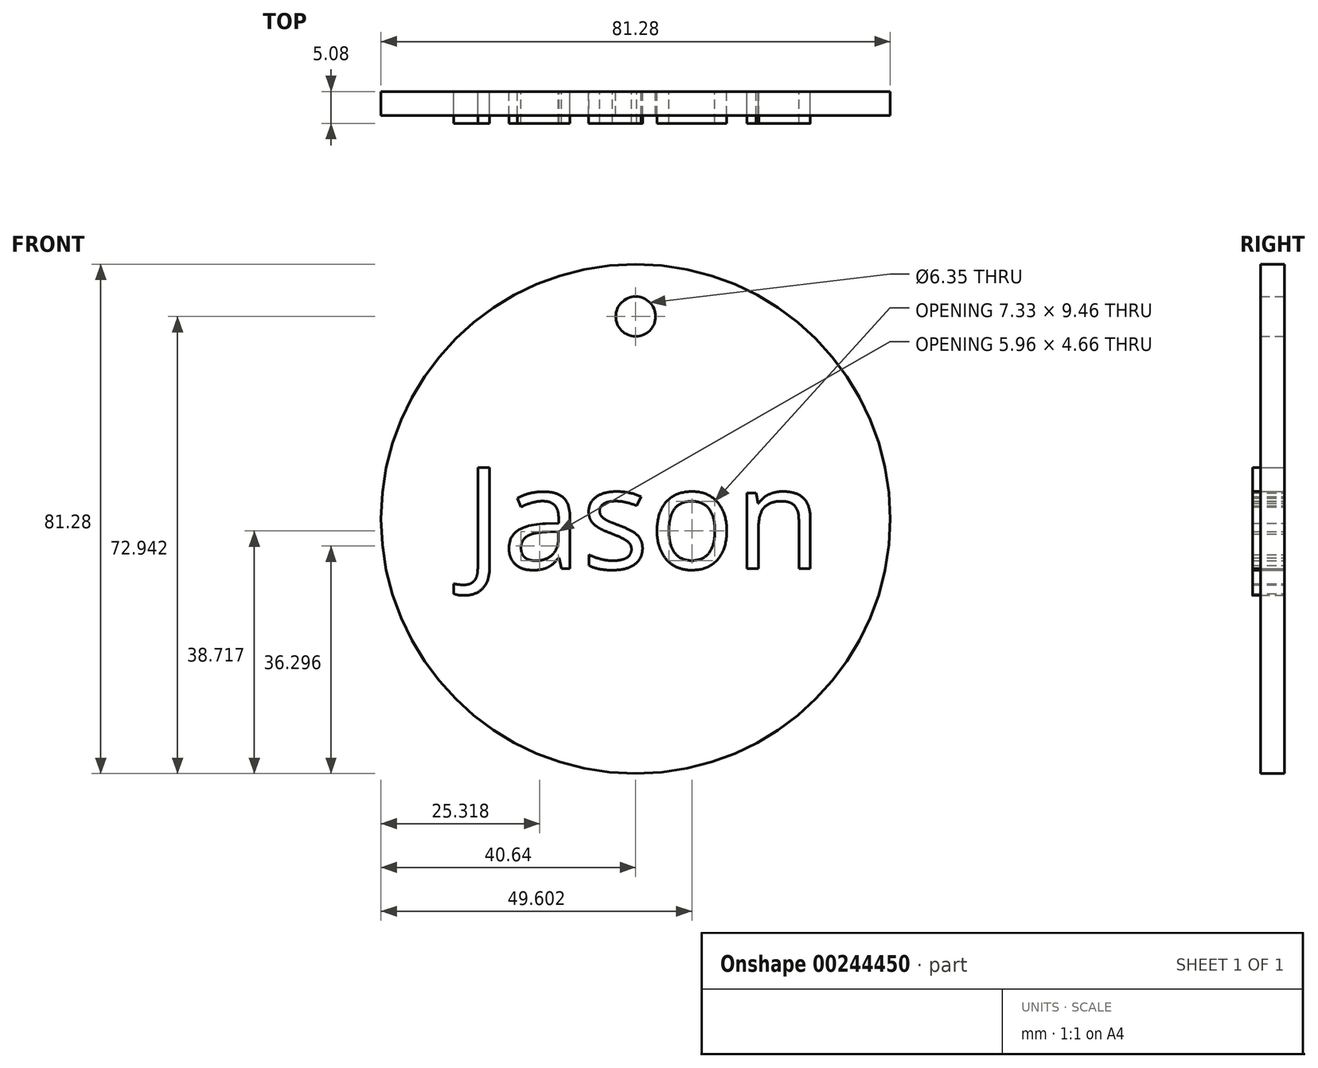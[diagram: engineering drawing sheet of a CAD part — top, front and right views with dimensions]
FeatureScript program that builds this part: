
annotation { "Feature Type Name" : "Feature", "Feature Type Description" : "" }
export const myFeature = defineFeature(function(context is Context, id is Id, definition is map)
    precondition{}
    {
        {
            var Q0;
            Q0=qCreatedBy(makeId("Front.planeOp"),FACE);
            var sketch = newSketch(context, id + "F0", { "sketchPlane" : qUnion([Q0])});
            skText(sketch, "E0", { "text": "Jason\n", "fontName": "OpenSans-Regular.ttf"});
            const initialGuessF0  = {"E0": [-0.02731, -0.00797, 1, 0, 0.0163]};
            skSetInitialGuess(sketch, initialGuessF0);
            skSolve(sketch);
        }
        {
            var Q0;
            Q0 = qSketchRegion(id + "F0", true);
            extrude(context, id + "F1", {"entities" : qUnion([Q0]), "depth" : 5.08 * mm});
        }
        {
            var Q0;
            Q0=qCreatedBy(makeId("Front.planeOp"),FACE);
            var sketch = newSketch(context, id + "F2", { "sketchPlane" : qUnion([Q0])});
            skCircle(sketch, "E1", {"center": v(0, 0) * mm, "radius": 40.64 * mm});
            skSolve(sketch);
        }
        {
            var Q0;
            Q0=makeQuery(id+"F2.imprint","IMPRINT",FACE,{"disambiguationData":[TD([[makeQuery(id+"F2.imprint","IMPRINT",EDGE,{"derivedFrom":sQuery(id+"F2.wireOp",EDGE,"E1")}),1.0]])]});
            extrude(context, id + "F3", {"entities" : qUnion([Q0]), "depth" : 3.8 * mm});
        }
        {
            var Q0;
            Q0=qCreatedBy(makeId("Front.planeOp"),FACE);
            var sketch = newSketch(context, id + "F4", { "sketchPlane" : qUnion([Q0])});
            skCircle(sketch, "E2", {"center": v(0, 32.3) * mm, "radius": 4.2 * mm});
            skSolve(sketch);
        }
        {
            var Q0;
            Q0=sQuery(id+"F4.wireOp",VERTEX,"E2.center");
            var Q1;
            Q1=makeQuery(id+"F3.opExtrude","SWEPT_BODY",BODY,{"disambiguationData":[OSD([sQuery(id+"F2.wireOp",EDGE,"E1")])]});
            hole(context, id + "F5", {"style" : HoleStyle.SIMPLE, "endStyle" : HoleEndStyle.THROUGH, "oppositeDirection" : true, "holeDiameter" : 6.35 * mm, "tappedDepth" : 12.7 * mm, "tapClearance" : 3, "locations" : qUnion([Q0]), "scope" : qUnion([Q1])});
        }
    });
